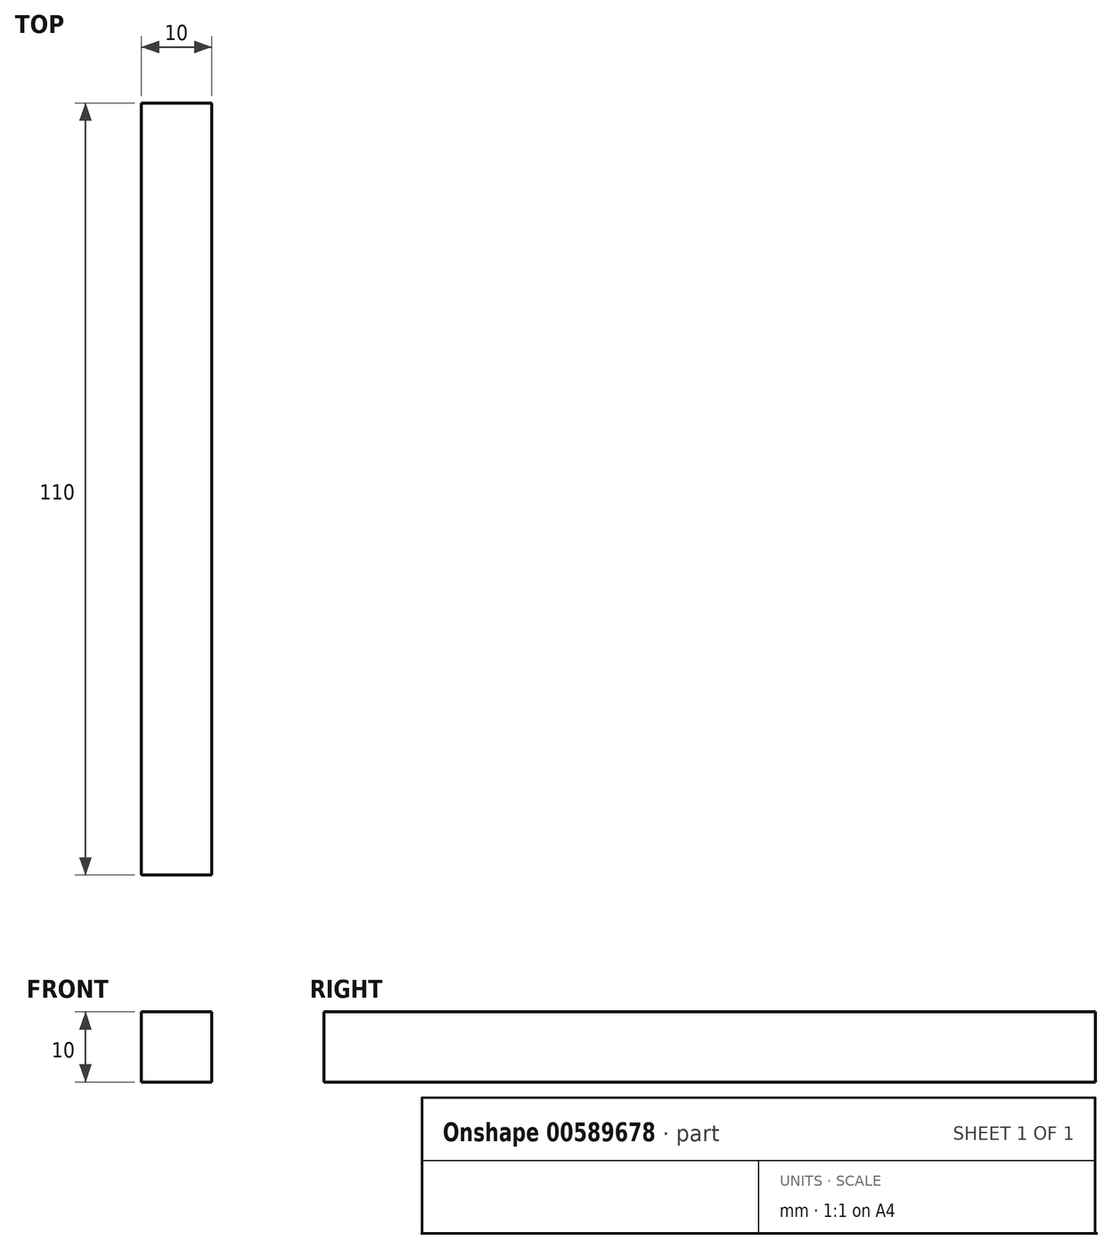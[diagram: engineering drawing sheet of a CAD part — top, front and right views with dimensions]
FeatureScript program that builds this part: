
annotation { "Feature Type Name" : "Feature", "Feature Type Description" : "" }
export const myFeature = defineFeature(function(context is Context, id is Id, definition is map)
    precondition{}
    {
        {
            var Q0;
            Q0=qCreatedBy(makeId("Front.planeOp"),FACE);
            var sketch = newSketch(context, id + "F0", { "sketchPlane" : qUnion([Q0])});
            skLineSegment(sketch, "E0", {"start": v(0, 5) * mm, "end": v(-5, 5) * mm});
            skLineSegment(sketch, "E1", {"start": v(-5, 5) * mm, "end": v(-5, 0) * mm});
            skLineSegment(sketch, "E2.MirrorCS", {"start": v(0, 5) * mm, "end": v(5, 5) * mm});
            skLineSegment(sketch, "E3.MirrorCS", {"start": v(5, 5) * mm, "end": v(5, 0) * mm});
            skLineSegment(sketch, "E4.MirrorCS", {"start": v(0, -5) * mm, "end": v(5, -5) * mm});
            skLineSegment(sketch, "E5.MirrorCS", {"start": v(5, -5) * mm, "end": v(5, 0) * mm});
            skLineSegment(sketch, "E6.MirrorCS", {"start": v(0, -5) * mm, "end": v(-5, -5) * mm});
            skLineSegment(sketch, "E7.MirrorCS", {"start": v(-5, -5) * mm, "end": v(-5, 0) * mm});
            skSolve(sketch);
        }
        {
            var Q0;
            Q0=makeQuery(id+"F0.imprint","IMPRINT",FACE,{"disambiguationData":[TD([[makeQuery(id+"F0.imprint","IMPRINT",EDGE,{"derivedFrom":sQuery(id+"F0.wireOp",EDGE,"E0")}),1.0]])]});
            extrude(context, id + "F1", {"entities" : qUnion([Q0]), "endBound" : BoundingType.SYMMETRIC, "depth" : 110 * mm, "offsetDistance" : 25 * mm});
        }
    });
